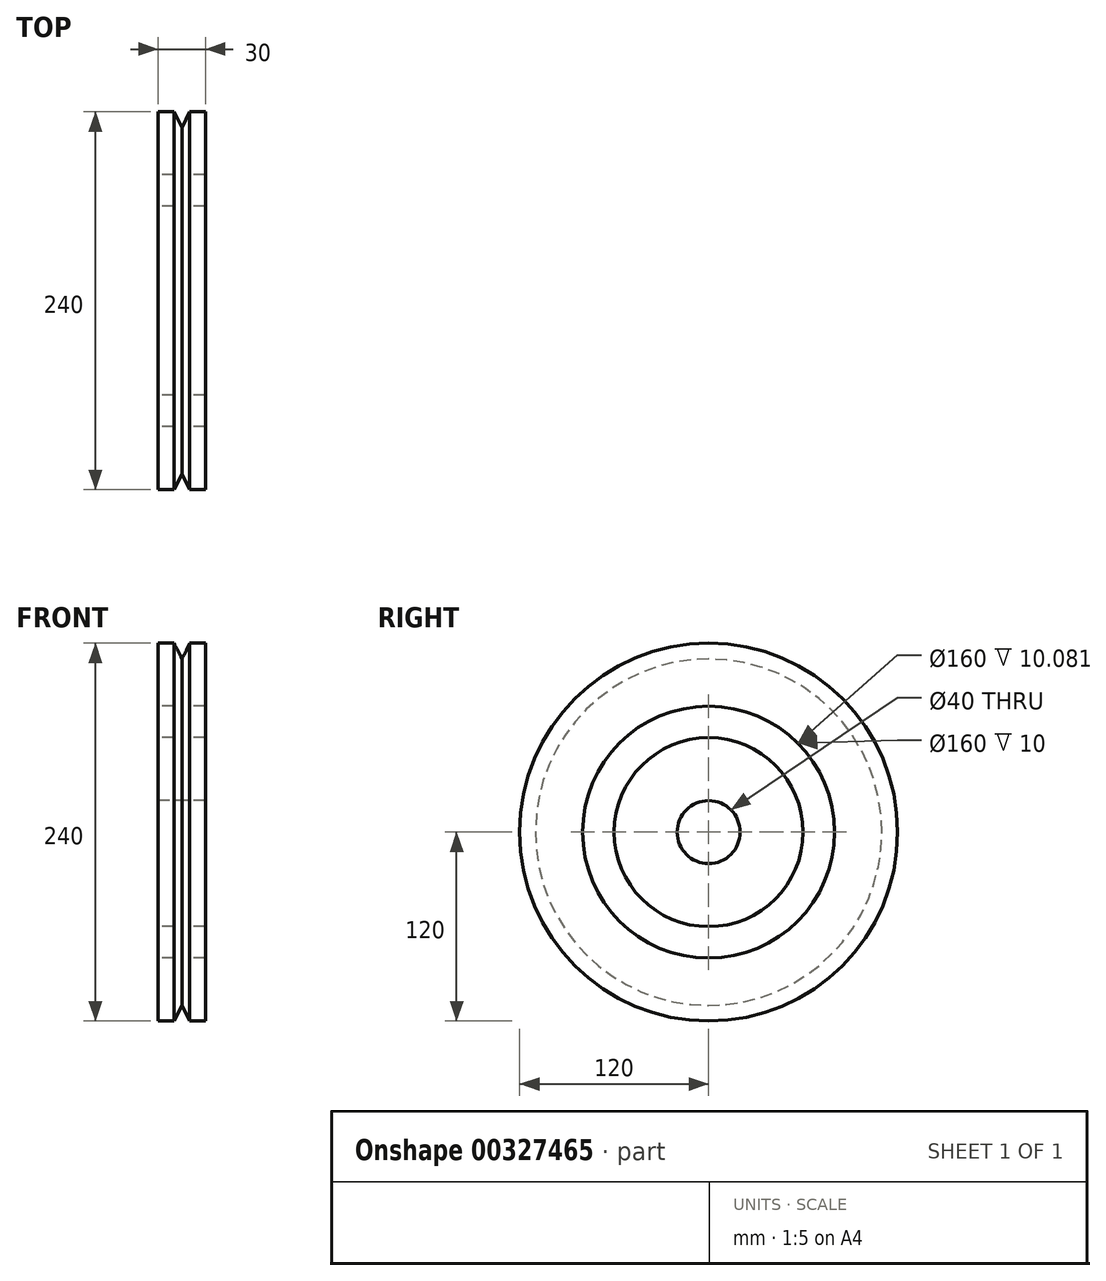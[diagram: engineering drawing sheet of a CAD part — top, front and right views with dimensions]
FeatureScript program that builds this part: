
annotation { "Feature Type Name" : "Feature", "Feature Type Description" : "" }
export const myFeature = defineFeature(function(context is Context, id is Id, definition is map)
    precondition{}
    {
        {
            var Q0;
            Q0=qCreatedBy(makeId("Front.planeOp"),FACE);
            var sketch = newSketch(context, id + "F0", { "sketchPlane" : qUnion([Q0])});
            skLineSegment(sketch, "E0", {"start": v(-28.89, 0) * mm, "end": v(33.7, 0) * mm});
            skLineSegment(sketch, "E1", {"start": v(0, 0) * mm, "end": v(0, -20) * mm});
            skLineSegment(sketch, "E2", {"start": v(0, -20) * mm, "end": v(0, -20) * mm});
            skLineSegment(sketch, "E3", {"start": v(0, -20) * mm, "end": v(0, -60) * mm});
            skLineSegment(sketch, "E4", {"start": v(0, -60) * mm, "end": v(-10, -60) * mm});
            skLineSegment(sketch, "E5", {"start": v(0, -110) * mm, "end": v(0, -120) * mm});
            skLineSegment(sketch, "E6", {"start": v(0, -120) * mm, "end": v(-30, -120) * mm});
            skLineSegment(sketch, "E7", {"start": v(-30, -120) * mm, "end": v(-30, -80) * mm});
            skLineSegment(sketch, "E8", {"start": v(-30, -80) * mm, "end": v(-20, -80) * mm});
            skLineSegment(sketch, "E9", {"start": v(-20, -80) * mm, "end": v(-20, -60) * mm});
            skLineSegment(sketch, "E10", {"start": v(-20, -60) * mm, "end": v(-30, -60) * mm});
            skLineSegment(sketch, "E11", {"start": v(-30, -60) * mm, "end": v(-30, -20) * mm});
            skLineSegment(sketch, "E12", {"start": v(-30, -20) * mm, "end": v(0, -20) * mm});
            skLineSegment(sketch, "E13", {"start": v(0, -110) * mm, "end": v(0, -80) * mm});
            skLineSegment(sketch, "E14", {"start": v(0, -80) * mm, "end": v(-10.08, -80) * mm});
            skLineSegment(sketch, "E15", {"start": v(-10.08, -80) * mm, "end": v(-10, -60) * mm});
            skLineSegment(sketch, "E16", {"start": v(-20, -120) * mm, "end": v(-30, -120) * mm});
            skLineSegment(sketch, "E17", {"start": v(-15, -120) * mm, "end": v(-15, -110) * mm});
            skLineSegment(sketch, "E18", {"start": v(-10.08, -120) * mm, "end": v(-15, -110) * mm});
            skLineSegment(sketch, "E19", {"start": v(-15, -110) * mm, "end": v(-20, -120) * mm});
            skSolve(sketch);
        }
        {
            var Q0;
            Q0=makeQuery(id+"F0.imprint","IMPRINT",FACE,{"disambiguationData":[TD([[makeQuery(id+"F0.imprint","IMPRINT",EDGE,{"derivedFrom":sQuery(id+"F0.wireOp",EDGE,"E3")}),-1.0]])]});
            var Q1;
            Q1=sQuery(id+"F0.wireOp",EDGE,"E0");
            revolve(context, id + "F1", {"entities" : qUnion([Q0]), "axis" : qUnion([Q1]), "revolveType" : RevolveType.FULL});
        }
    });
